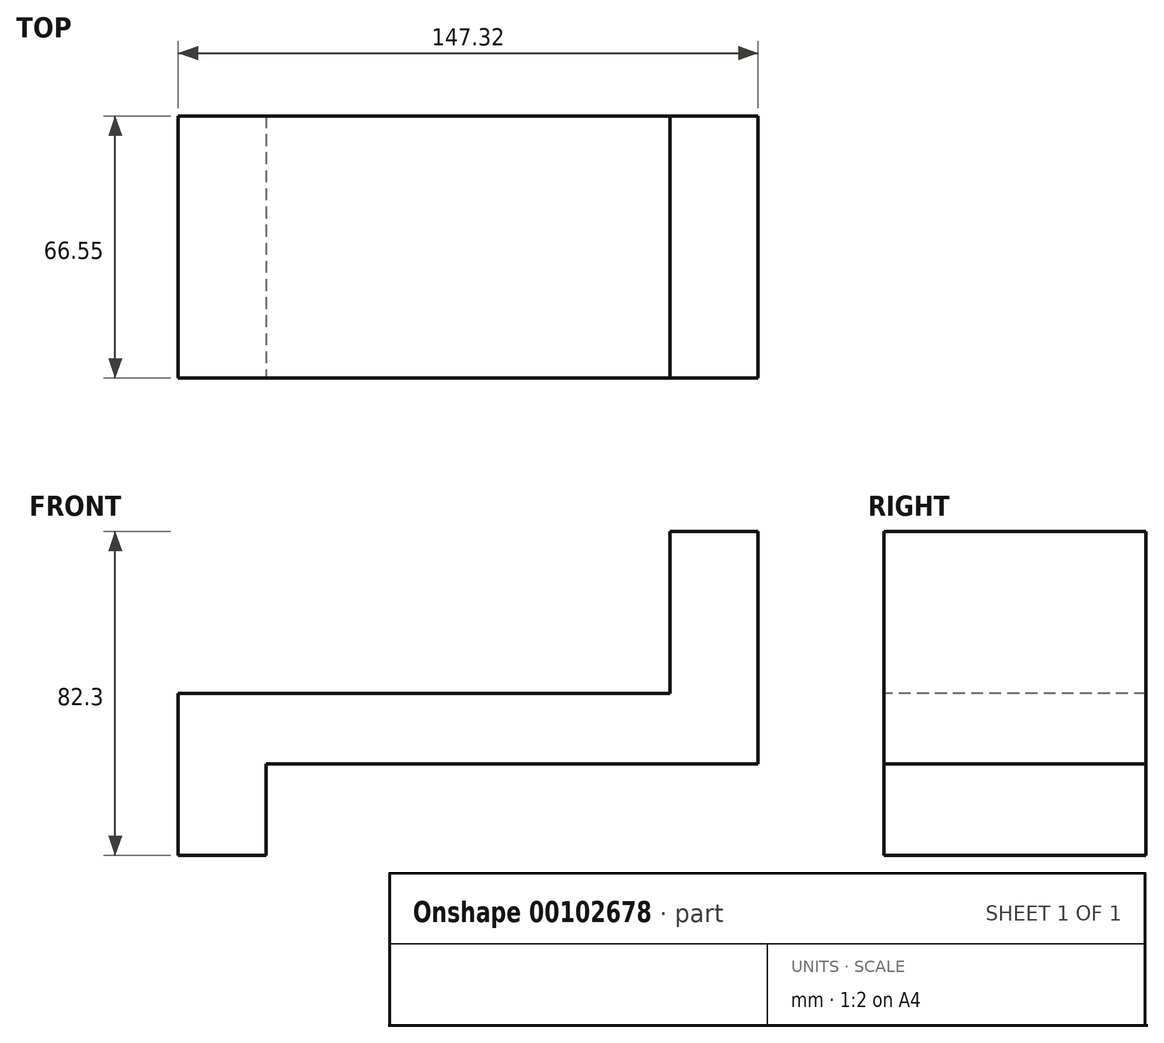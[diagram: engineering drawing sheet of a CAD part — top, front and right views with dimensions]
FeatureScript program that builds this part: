
annotation { "Feature Type Name" : "Feature", "Feature Type Description" : "" }
export const myFeature = defineFeature(function(context is Context, id is Id, definition is map)
    precondition{}
    {
        {
            var Q0;
            Q0=qCreatedBy(makeId("Top.planeOp"),FACE);
            var sketch = newSketch(context, id + "F0", { "sketchPlane" : qUnion([Q0])});
            skLineSegment(sketch, "E0.bottom", {"start": v(-107.3, 32.7) * mm, "end": v(40.01, 32.7) * mm});
            skLineSegment(sketch, "E0.top", {"start": v(-107.3, -33.85) * mm, "end": v(40.01, -33.85) * mm});
            skLineSegment(sketch, "E0.left", {"start": v(-107.3, 32.7) * mm, "end": v(-107.3, -33.85) * mm});
            skLineSegment(sketch, "E0.right", {"start": v(40.01, 32.7) * mm, "end": v(40.01, -33.85) * mm});
            skSolve(sketch);
        }
        {
            var Q0;
            Q0 = qSketchRegion(id + "F0", true);
            extrude(context, id + "F1", {"entities" : qUnion([Q0]), "depth" : 82.3 * mm});
        }
        {
            var Q0;
            Q0=makeQuery(id+"F1.opExtrude","SWEPT_FACE",FACE,{"disambiguationData":[OSD([sQuery(id+"F0.wireOp",EDGE,"E0.right")])]});
            var sketch = newSketch(context, id + "F2", { "sketchPlane" : qUnion([Q0])});
            skLineSegment(sketch, "E1.bottom", {"start": v(-33.85, 0) * mm, "end": v(32.7, 0) * mm});
            skLineSegment(sketch, "E1.top", {"start": v(-33.85, 23.2) * mm, "end": v(32.7, 23.2) * mm});
            skLineSegment(sketch, "E1.left", {"start": v(-33.85, 0) * mm, "end": v(-33.85, 23.2) * mm});
            skLineSegment(sketch, "E1.right", {"start": v(32.7, 0) * mm, "end": v(32.7, 23.2) * mm});
            skSolve(sketch);
        }
        {
            var Q0;
            Q0 = qSketchRegion(id + "F2", true);
            extrude(context, id + "F3", {"entities" : qUnion([Q0]), "operationType" : NewBodyOperationType.REMOVE, "oppositeDirection" : true, "depth" : 124.97 * mm});
        }
        {
            var Q0;
            Q0=makeQuery(id+"F1.opExtrude","SWEPT_FACE",FACE,{"disambiguationData":[OSD([sQuery(id+"F0.wireOp",EDGE,"E0.left")])]});
            var sketch = newSketch(context, id + "F4", { "sketchPlane" : qUnion([Q0])});
            skLineSegment(sketch, "E2.bottom", {"start": v(-32.7, 82.3) * mm, "end": v(33.85, 82.3) * mm});
            skLineSegment(sketch, "E2.top", {"start": v(-32.7, 41.15) * mm, "end": v(33.85, 41.15) * mm});
            skLineSegment(sketch, "E2.left", {"start": v(-32.7, 82.3) * mm, "end": v(-32.7, 41.15) * mm});
            skLineSegment(sketch, "E2.right", {"start": v(33.85, 82.3) * mm, "end": v(33.85, 41.15) * mm});
            skSolve(sketch);
        }
        {
            var Q0;
            Q0 = qSketchRegion(id + "F4", true);
            extrude(context, id + "F5", {"entities" : qUnion([Q0]), "operationType" : NewBodyOperationType.REMOVE, "oppositeDirection" : true, "depth" : 124.97 * mm});
        }
    });
